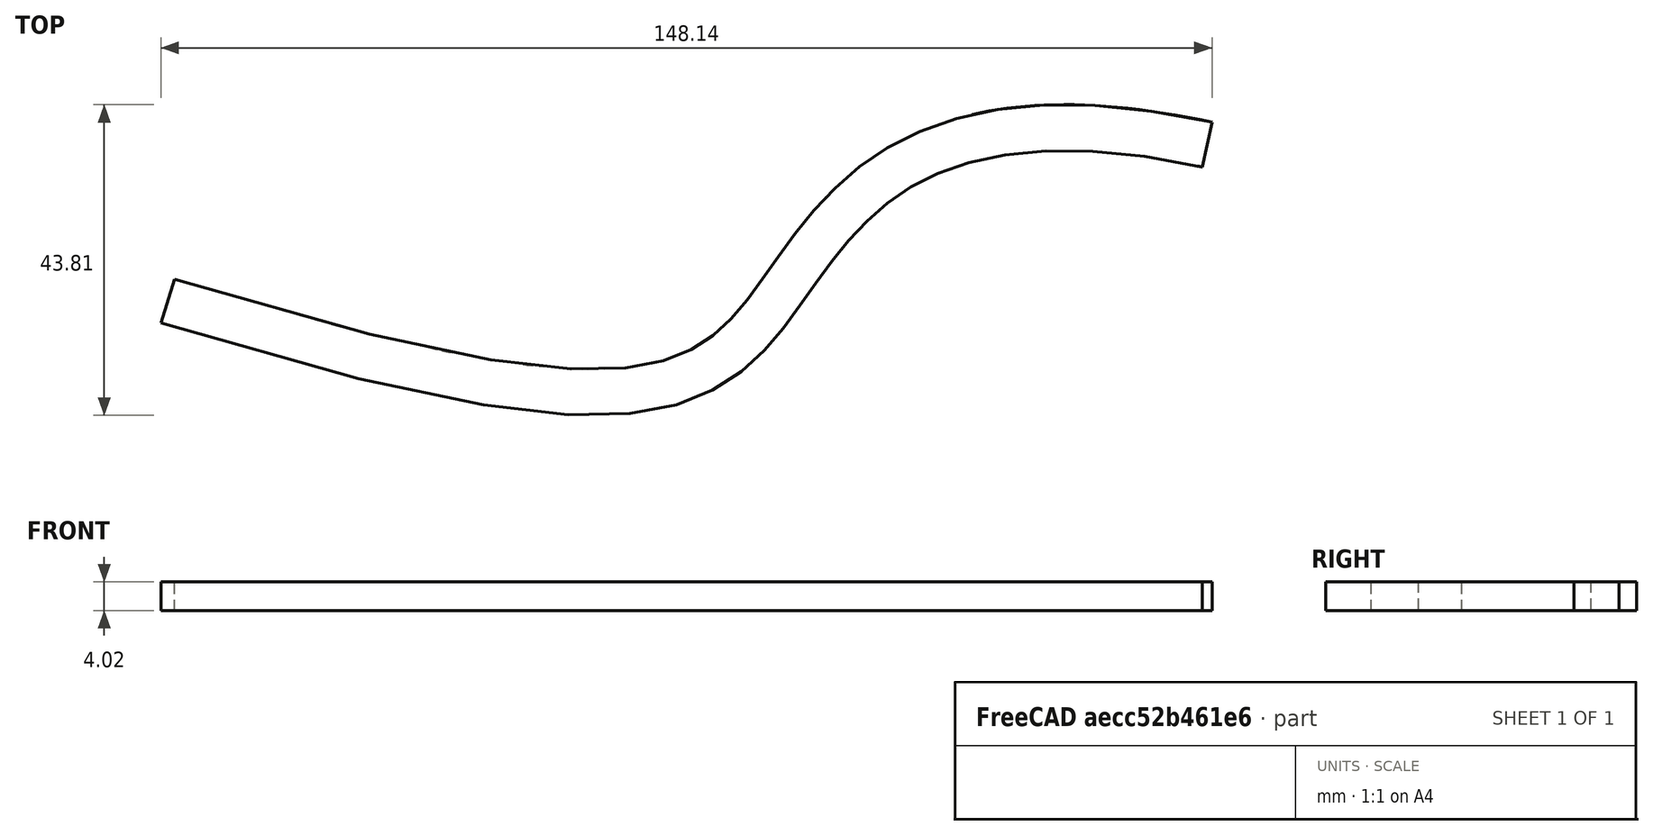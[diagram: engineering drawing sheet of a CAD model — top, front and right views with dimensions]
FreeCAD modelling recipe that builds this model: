
FCSTD DOCUMENT  (FreeCAD 0.17R13217 (Git))
Label: 13-extrusion-trayectoria
License: All rights reserved
LicenseURL: http://en.wikipedia.org/wiki/All_rights_reserved
objects: Sketcher::SketchObject×2, PartDesign::Plane×1, PartDesign::AdditivePipe×1, PartDesign::Body×1
note: 6 computed .brp shape members not serialized (recipe doc carries the construction recipe); baked Part::Feature solids carry a one-line shape summary decoded from their .brp

FEATURE [Sketcher::SketchObject] Sketch
  MapMode = 5
  Support = -> [XY_Plane]
  sketch-geometry (7):
    g0-g3: Circle [constr] x4 (B-spline internal-alignment scaffolding for g4; pole/knot coordinates omitted)
    g4: BSplineCurve PolesCount=4 KnotsCount=2 Degree=3 IsPeriodic=0
    g5: GeomPoint [constr] X=-71.9843 Y=-16.9945 Z=0
    g6: GeomPoint [constr] X=74.5156 Y=5.07664 Z=0
  constraints (3):
    c: InternalAlignment(g0-g3 -> g4) x4
    c: InternalAlignment(g5,g4)
    c: InternalAlignment(g6,g4)
FEATURE [PartDesign::Plane] DatumPlane
  MapMode = 8
  Placement = pos=(-71.9843,-16.9945,0) rot=(-0.462949,0.626769,0.626769;4.00873rad)
  Support = -> [Sketch]
FEATURE [Sketcher::SketchObject] Sketch001
  MapMode = 5
  Placement = pos=(-71.9843,-16.9945,0) rot=(-0.462949,0.626769,0.626769;4.00873rad)
  Support = -> [DatumPlane]
  sketch-geometry (4):
    g0: LineSegment StartX=-3.23144 StartY=2.00882 StartZ=0 EndX=3.23144 EndY=2.00882 EndZ=0
    g1: LineSegment StartX=3.23144 StartY=2.00882 StartZ=0 EndX=3.23144 EndY=-2.00882 EndZ=0
    g2: LineSegment StartX=3.23144 StartY=-2.00882 StartZ=0 EndX=-3.23144 EndY=-2.00882 EndZ=0
    g3: LineSegment StartX=-3.23144 StartY=-2.00882 StartZ=0 EndX=-3.23144 EndY=2.00882 EndZ=0
  constraints (9):
    c: Coincident(g0,g1)
    c: Coincident(g1,g2)
    c: Coincident(g2,g3)
    c: Coincident(g3,g0)
    c: Horizontal(g0)
    c: Horizontal(g2)
    c: Vertical(g1)
    c: Vertical(g3)
    c: Symmetric(g0,g1,g-1)
FEATURE [PartDesign::AdditivePipe] AdditivePipe
  AuxilleryCurvelinear = true
  AuxillerySpineTangent = false
  Binormal = (0,0,0)
  Mode = 0
  Placement = pos=(-71.9843,-16.9945,0) rot=(-0.462949,0.626769,0.626769;4.00873rad)
  Profile = -> Sketch001
  Refine = true
  Spine = -> Sketch
  SpineTangent = false
  Transformation = 0
  Transition = 0
FEATURE [PartDesign::Body] Body
  Group = -> [Sketch,DatumPlane,Sketch001,AdditivePipe]
  Origin = -> Origin
  Tip = -> AdditivePipe
